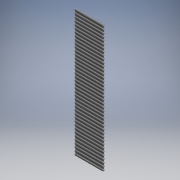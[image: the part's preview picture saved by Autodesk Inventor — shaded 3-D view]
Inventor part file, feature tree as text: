
AUTODESK INVENTOR PART (.ipt)
format: ipt  version: 2017.3 (Build 213256000, 256)  size: 427,008 bytes
history: native  units: mm (DEFAULTED — no unit token found)
features: other x14, sketch x2, extrude x1, revolve x1
ambient origin geometry x8: Origin, YZ Plane, XZ Plane, XY Plane, X Axis, Y Axis, Z Axis, Center Point
bodies: Solid1 (feature_tree)
feature tree (18):
  extrude  "Extrusion1"  TaperAngle=180.0deg  [1 undecoded]
  revolve  "Revolution1"  [1 undecoded]
  other  "cable_to_dummy_XY"
  other  "cable_to_dummy_YZ"
  other  "cable_to_dummy_ZX"
  other  "cable_to_dummy_X"
  other  "cable_to_dummy_Y"
  other  "cable_to_dummy_Z"
  other  "cable_to_dummy_Center"
  other  "cable_to_lower_body_XY"
  other  "cable_to_lower_body_YZ"
  other  "cable_to_lower_body_ZX"
  other  "cable_to_lower_body_X"
  other  "cable_to_lower_body_Y"
  other  "cable_to_lower_body_Z"
  other  "cable_to_lower_body_Center"
  sketch  "Sketch_1"  dims[d0=10.9855mm d1=0.0mm d2=180.0deg]
  sketch  "Sketch_2"
note: 2 required parameter values undecoded (feature->parameter linkage not recoverable at this tier; creation-order binding heuristic only, values carry confidence <= 0.55)
